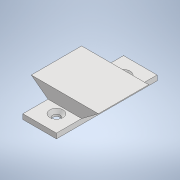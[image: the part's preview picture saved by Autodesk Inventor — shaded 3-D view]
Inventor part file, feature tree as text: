
AUTODESK INVENTOR PART (.ipt)
format: ipt  version: 2022.3 (Build 263350000, 350)  size: 120,832 bytes
history: native  units: mm
features: sketch x3, extrude x2, hole x1
ambient origin geometry x8: Origin, YZ Plane, XZ Plane, XY Plane, X Axis, Y Axis, Z Axis, Center Point
bodies: Solid1 (feature_tree)
feature tree (6):
  extrude  "Extrusion1"  Depth=30.0mm
  hole  "Hole1"  [1 undecoded]
  extrude  "Extrusion2"  Depth=7.5mm
  sketch  "Sketch1"  dims[d0=10.0mm d1=30.0mm]
  sketch  "Sketch2"  dims[d2=1.5mm d3=0.0mm d4=10.0mm]
  sketch  "Sketch3"  dims[d5=20.0mm d6=2.2mm d7=6.0mm d8=4.0mm d9=2.0mm d10=90.0deg d11=0.9mm d12=0.0mm d13=20.0mm d14=7.5mm d15=7.5mm d16=7.5mm d17=0.0mm d18=0.0mm]
note: 1 required parameter value undecoded (feature->parameter linkage not recoverable at this tier; creation-order binding heuristic only, values carry confidence <= 0.55)
